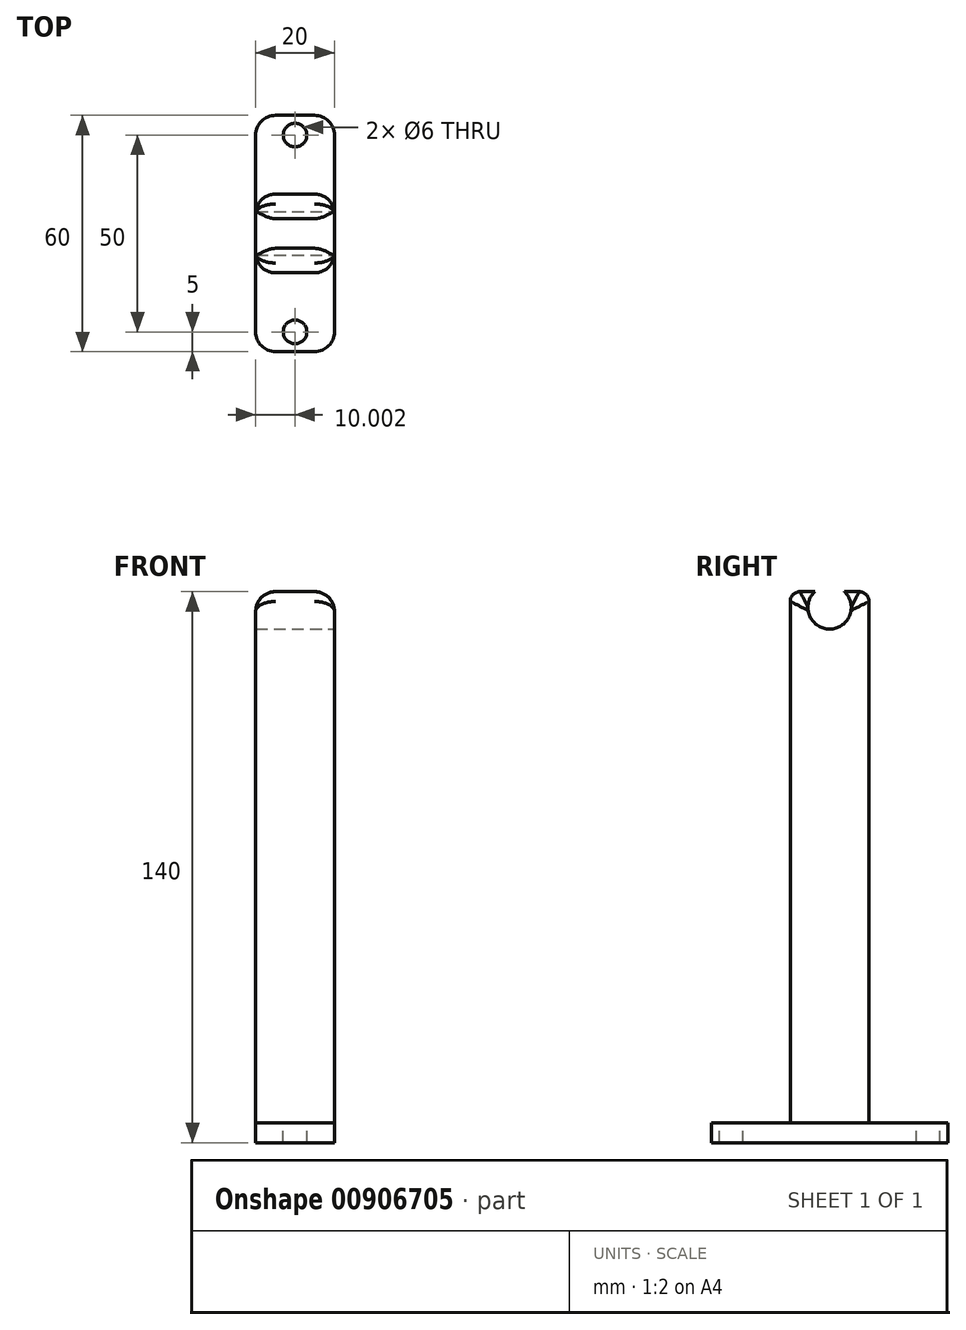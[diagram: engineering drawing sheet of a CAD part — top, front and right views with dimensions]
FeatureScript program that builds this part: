
annotation { "Feature Type Name" : "Feature", "Feature Type Description" : "" }
export const myFeature = defineFeature(function(context is Context, id is Id, definition is map)
    precondition{}
    {
        {
            var Q0;
            Q0=qCreatedBy(makeId("Top.planeOp"),FACE);
            var sketch = newSketch(context, id + "F0", { "sketchPlane" : qUnion([Q0])});
            skLineSegment(sketch, "E0.right", {"start": v(75.78, -37.5) * mm, "end": v(75.78, 22.5) * mm});
            skLineSegment(sketch, "E1", {"start": v(55.78, -37.5) * mm, "end": v(75.78, -37.5) * mm});
            skLineSegment(sketch, "E2", {"start": v(55.78, 22.5) * mm, "end": v(75.78, 22.5) * mm});
            skLineSegment(sketch, "E3", {"start": v(65.78, 22.5) * mm, "end": v(65.78, -37.5) * mm, "construction": true});
            skLineSegment(sketch, "E4", {"start": v(55.78, -37.5) * mm, "end": v(55.78, 22.5) * mm});
            skSolve(sketch);
        }
        {
            var Q0;
            Q0 = qSketchRegion(id + "F0", true);
            var Q1;
            Q1=makeQuery(id+"F0.imprint","IMPRINT",FACE,{"disambiguationData":[TD([[makeQuery(id+"F0.imprint","IMPRINT",EDGE,{"derivedFrom":sQuery(id+"F0.wireOp",EDGE,"E0.bottom")}),1.0]])]});
            extrude(context, id + "F1", {"entities" : qUnion([Q0, Q1]), "depth" : 5 * mm, "offsetDistance" : 25 * mm});
        }
        {
            var Q0;
            Q0=makeQuery(id+"F1.opExtrude","SWEPT_EDGE",EDGE,{"disambiguationData":[OSD([sQuery(id+"F0.wireOp",EDGE,"E0.left"),sQuery(id+"F0.wireOp",EDGE,"nmI8195d-Xumq-3xWw-G374-Udysf1wdiRkK")])]});
            var Q1;
            Q1=makeQuery(id+"F1.opExtrude","SWEPT_EDGE",EDGE,{"disambiguationData":[OSD([sQuery(id+"F0.wireOp",EDGE,"E0.right"),sQuery(id+"F0.wireOp",EDGE,"E2")])]});
            var Q2;
            Q2=makeQuery(id+"F1.opExtrude","SWEPT_EDGE",EDGE,{"disambiguationData":[OSD([sQuery(id+"F0.wireOp",EDGE,"E0.right"),sQuery(id+"F0.wireOp",EDGE,"E1")])]});
            var Q3;
            Q3=makeQuery(id+"F1.opExtrude","SWEPT_EDGE",EDGE,{"disambiguationData":[OSD([sQuery(id+"F0.wireOp",EDGE,"nmI8195d-Xumq-3xWw-G374-Udysf1wdiRkK"),sQuery(id+"F0.wireOp",EDGE,"3TTH9Oto-mKUP-eSFD-OSz8-A00A0DzyHvfx")])]});
            var Q4;
            Q4=makeQuery(id+"F1.opExtrude","SWEPT_EDGE",EDGE,{"disambiguationData":[OSD([sQuery(id+"F0.wireOp",EDGE,"NlstWC2O-AiH8-S6MD-4HLF-AFcN5YqJXIDJ"),sQuery(id+"F0.wireOp",EDGE,"4GDDCi85-TuiU-ghBi-D55u-NQaOYuRGezC8")])]});
            var Q5;
            Q5=makeQuery(id+"F1.opExtrude","SWEPT_EDGE",EDGE,{"disambiguationData":[OSD([sQuery(id+"F0.wireOp",EDGE,"E0.left"),sQuery(id+"F0.wireOp",EDGE,"NlstWC2O-AiH8-S6MD-4HLF-AFcN5YqJXIDJ")])]});
            var Q6;
            Q6=makeQuery(id+"F1.opExtrude","SWEPT_EDGE",EDGE,{"disambiguationData":[OSD([sQuery(id+"F0.wireOp",EDGE,"gAzKnPfo-PUQO-n0jp-SFb8-rANGOECkmPY2"),sQuery(id+"F0.wireOp",EDGE,"E2")])]});
            var Q7;
            Q7=makeQuery(id+"F1.opExtrude","SWEPT_EDGE",EDGE,{"disambiguationData":[OSD([sQuery(id+"F0.wireOp",EDGE,"LALdFzbi-xZhH-pntJ-odxi-O5FkvFgCXXKE"),sQuery(id+"F0.wireOp",EDGE,"E1")])]});
            fillet(context, id + "F2", {"entities" : qUnion([Q0, Q1, Q2, Q3, Q4, Q5, Q6, Q7]), "radius" : 5 * mm, "tangentPropagation" : true, "allowEdgeOverflow" : false});
        }
        {
            var Q0;
            Q0=makeQuery(id+"F1.opExtrude","CAP_FACE",FACE,{"disambiguationData":[OSD([sQuery(id+"F0.wireOp",EDGE,"E0.left"),sQuery(id+"F0.wireOp",EDGE,"E0.right"),sQuery(id+"F0.wireOp",EDGE,"nmI8195d-Xumq-3xWw-G374-Udysf1wdiRkK"),sQuery(id+"F0.wireOp",EDGE,"3TTH9Oto-mKUP-eSFD-OSz8-A00A0DzyHvfx"),sQuery(id+"F0.wireOp",EDGE,"LXfHk3JK-jXvN-s0UF-aqjt-Lvplc94hBw2p"),sQuery(id+"F0.wireOp",EDGE,"LALdFzbi-xZhH-pntJ-odxi-O5FkvFgCXXKE"),sQuery(id+"F0.wireOp",EDGE,"E1"),sQuery(id+"F0.wireOp",EDGE,"NlstWC2O-AiH8-S6MD-4HLF-AFcN5YqJXIDJ"),sQuery(id+"F0.wireOp",EDGE,"4GDDCi85-TuiU-ghBi-D55u-NQaOYuRGezC8"),sQuery(id+"F0.wireOp",EDGE,"qwk2k2DY-2ik6-FNbK-F8m8-Ih2qOiGvFig5"),sQuery(id+"F0.wireOp",EDGE,"gAzKnPfo-PUQO-n0jp-SFb8-rANGOECkmPY2"),sQuery(id+"F0.wireOp",EDGE,"E2")])],"isStart":false});
            var sketch = newSketch(context, id + "F3", { "sketchPlane" : qUnion([Q0])});
            skLineSegment(sketch, "E5", {"start": v(75.78, -7.5) * mm, "end": v(55.78, -7.5) * mm, "construction": true});
            skLineSegment(sketch, "E6.bottom", {"start": v(55.78, -17.5) * mm, "end": v(75.78, -17.5) * mm});
            skLineSegment(sketch, "E6.top", {"start": v(55.78, 2.5) * mm, "end": v(75.78, 2.5) * mm});
            skLineSegment(sketch, "E6.left", {"start": v(55.78, -17.5) * mm, "end": v(55.78, 2.5) * mm});
            skLineSegment(sketch, "E6.right", {"start": v(75.78, -17.5) * mm, "end": v(75.78, 2.5) * mm});
            skSolve(sketch);
        }
        {
            var Q0;
            Q0=makeQuery(id+"F3.imprint","IMPRINT",FACE,{"disambiguationData":[TD([[makeQuery(id+"F3.imprint","IMPRINT",EDGE,{"derivedFrom":sQuery(id+"F3.wireOp",EDGE,"E6.bottom")}),1.0]])]});
            extrude(context, id + "F4", {"entities" : qUnion([Q0]), "depth" : 135 * mm, "offsetDistance" : 25 * mm});
        }
        {
            var Q0;
            Q0=makeQuery(id+"FvWN4O11wuADM6J_2.boolean.opBoolean","MERGE",FACE,{"derivedFrom":[makeQuery(id+"F1.opExtrude","SWEPT_FACE",FACE,{"disambiguationData":[OSD([sQuery(id+"F0.wireOp",EDGE,"E0.right")])]}),makeQuery(id+"FvWN4O11wuADM6J_2.opExtrude","SWEPT_FACE",FACE,{"disambiguationData":[OSD([sQuery(id+"F3.wireOp",EDGE,"B9pi8wDC-0PHU-OhtB-8lwp-iYIqlVlSSCbZ.right")])]})]});
            var sketch = newSketch(context, id + "F5", { "sketchPlane" : qUnion([Q0])});
            skCircle(sketch, "E7", {"center": v(-7.5, 136) * mm, "radius": 7.5 * mm});
            skPoint(sketch, "E7.centerSnap0", {"position": v(-7.5, 130.5) * mm});
            skSolve(sketch);
        }
        {
            var Q0;
            Q0 = qSketchRegion(id + "F5", true);
            extrude(context, id + "F6", {"entities" : qUnion([Q0]), "operationType" : NewBodyOperationType.ADD, "oppositeDirection" : true, "depth" : 20 * mm, "offsetDistance" : 25 * mm});
        }
        {
            var Q0;
            Q0=makeQuery(id+"F6.boolean.opBoolean","MERGE",FACE,{"derivedFrom":[makeQuery(id+"FvWN4O11wuADM6J_2.boolean.opBoolean","MERGE",FACE,{"derivedFrom":[makeQuery(id+"F1.opExtrude","SWEPT_FACE",FACE,{"disambiguationData":[OSD([sQuery(id+"F0.wireOp",EDGE,"E0.right")])]}),makeQuery(id+"FvWN4O11wuADM6J_2.opExtrude","SWEPT_FACE",FACE,{"disambiguationData":[OSD([sQuery(id+"F3.wireOp",EDGE,"B9pi8wDC-0PHU-OhtB-8lwp-iYIqlVlSSCbZ.right")])]})]}),makeQuery(id+"F6.opExtrude","CAP_FACE",FACE,{"disambiguationData":[OSD([sQuery(id+"F5.wireOp",EDGE,"E7")])],"isStart":true})]});
            var sketch = newSketch(context, id + "F7", { "sketchPlane" : qUnion([Q0])});
            skCircle(sketch, "E8", {"center": v(-7.5, 136) * mm, "radius": 5.5 * mm});
            skSolve(sketch);
        }
        {
            var Q0;
            Q0=makeQuery(id+"F7.imprint","IMPRINT",FACE,{"disambiguationData":[TD([[makeQuery(id+"F7.imprint","IMPRINT",EDGE,{"derivedFrom":sQuery(id+"F7.wireOp",EDGE,"E8")}),1.0]])]});
            extrude(context, id + "F8", {"entities" : qUnion([Q0]), "operationType" : NewBodyOperationType.REMOVE, "oppositeDirection" : true, "depth" : 25 * mm, "offsetDistance" : 25 * mm});
        }
        {
            var Q0;
            Q0=makeQuery(id+"F4.opExtrude","CAP_EDGE",EDGE,{"disambiguationData":[OSD([sQuery(id+"F3.wireOp",EDGE,"E6.top")])],"isStart":false});
            var Q1;
            Q1=makeQuery(id+"F4.opExtrude","CAP_EDGE",EDGE,{"disambiguationData":[OSD([sQuery(id+"F3.wireOp",EDGE,"E6.bottom")])],"isStart":false});
            fillet(context, id + "F9", {"entities" : qUnion([Q0, Q1]), "tangentPropagation" : true, "radius" : 2.5 * mm, "defaultsChanged" : false, "vertexSettings" : [], "allowEdgeOverflow" : false});
        }
        {
            var Q0;
            Q0=makeQuery(id+"F4.opExtrude","SWEPT_FACE",FACE,{"disambiguationData":[OSD([sQuery(id+"F3.wireOp",EDGE,"E6.right")])]});
            var sketch = newSketch(context, id + "F10", { "sketchPlane" : qUnion([Q0])});
            skLineSegment(sketch, "E9.bottom", {"start": v(-15, 140) * mm, "end": v(0, 140) * mm});
            skLineSegment(sketch, "E9.top", {"start": v(-15, 145.46) * mm, "end": v(0, 145.46) * mm});
            skLineSegment(sketch, "E9.left", {"start": v(-15, 140) * mm, "end": v(-15, 145.46) * mm});
            skLineSegment(sketch, "E9.right", {"start": v(0, 140) * mm, "end": v(0, 145.46) * mm});
            skSolve(sketch);
        }
        {
            var Q0;
            Q0 = qSketchRegion(id + "F10", true);
            extrude(context, id + "F11", {"entities" : qUnion([Q0]), "operationType" : NewBodyOperationType.REMOVE, "oppositeDirection" : true, "depth" : 25 * mm, "offsetDistance" : 25 * mm});
        }
        {
            var Q0;
            Q0=makeQuery(id+"F4.opExtrude","SWEPT_EDGE",EDGE,{"disambiguationData":[OSD([sQuery(id+"F0.wireOp",EDGE,"E0.right"),sQuery(id+"F3.wireOp",EDGE,"E6.bottom"),sQuery(id+"F3.wireOp",EDGE,"E6.right")])]});
            var Q1;
            Q1=makeQuery(id+"F4.opExtrude","SWEPT_EDGE",EDGE,{"disambiguationData":[OSD([sQuery(id+"F0.wireOp",EDGE,"E4"),sQuery(id+"F3.wireOp",EDGE,"E6.top"),sQuery(id+"F3.wireOp",EDGE,"E6.left")])]});
            var Q2;
            Q2=makeQuery(id+"F4.opExtrude","SWEPT_EDGE",EDGE,{"disambiguationData":[OSD([sQuery(id+"F0.wireOp",EDGE,"E0.right"),sQuery(id+"F3.wireOp",EDGE,"E6.top"),sQuery(id+"F3.wireOp",EDGE,"E6.right")])]});
            var Q3;
            Q3=makeQuery(id+"F4.opExtrude","SWEPT_EDGE",EDGE,{"disambiguationData":[OSD([sQuery(id+"F0.wireOp",EDGE,"E4"),sQuery(id+"F3.wireOp",EDGE,"E6.bottom"),sQuery(id+"F3.wireOp",EDGE,"E6.left")])]});
            fillet(context, id + "F12", {"entities" : qUnion([Q0, Q1, Q2, Q3]), "tangentPropagation" : true, "radius" : 5 * mm, "defaultsChanged" : false, "vertexSettings" : [], "allowEdgeOverflow" : false});
        }
        {
            var Q0;
            Q0=makeQuery(id+"F1.opExtrude","CAP_FACE",FACE,{"disambiguationData":[OSD([sQuery(id+"F0.wireOp",EDGE,"E0.right"),sQuery(id+"F0.wireOp",EDGE,"E1"),sQuery(id+"F0.wireOp",EDGE,"E2"),sQuery(id+"F0.wireOp",EDGE,"E4")])],"isStart":false});
            var sketch = newSketch(context, id + "F13", { "sketchPlane" : qUnion([Q0])});
            skCircle(sketch, "E10", {"center": v(65.78, -32.5) * mm, "radius": 3 * mm});
            skCircle(sketch, "E11", {"center": v(65.78, 17.5) * mm, "radius": 3 * mm});
            skSolve(sketch);
        }
        {
            var Q0;
            Q0 = qSketchRegion(id + "F13", true);
            extrude(context, id + "F14", {"entities" : qUnion([Q0]), "operationType" : NewBodyOperationType.REMOVE, "oppositeDirection" : true, "depth" : 5 * mm, "offsetDistance" : 25 * mm});
        }
    });
